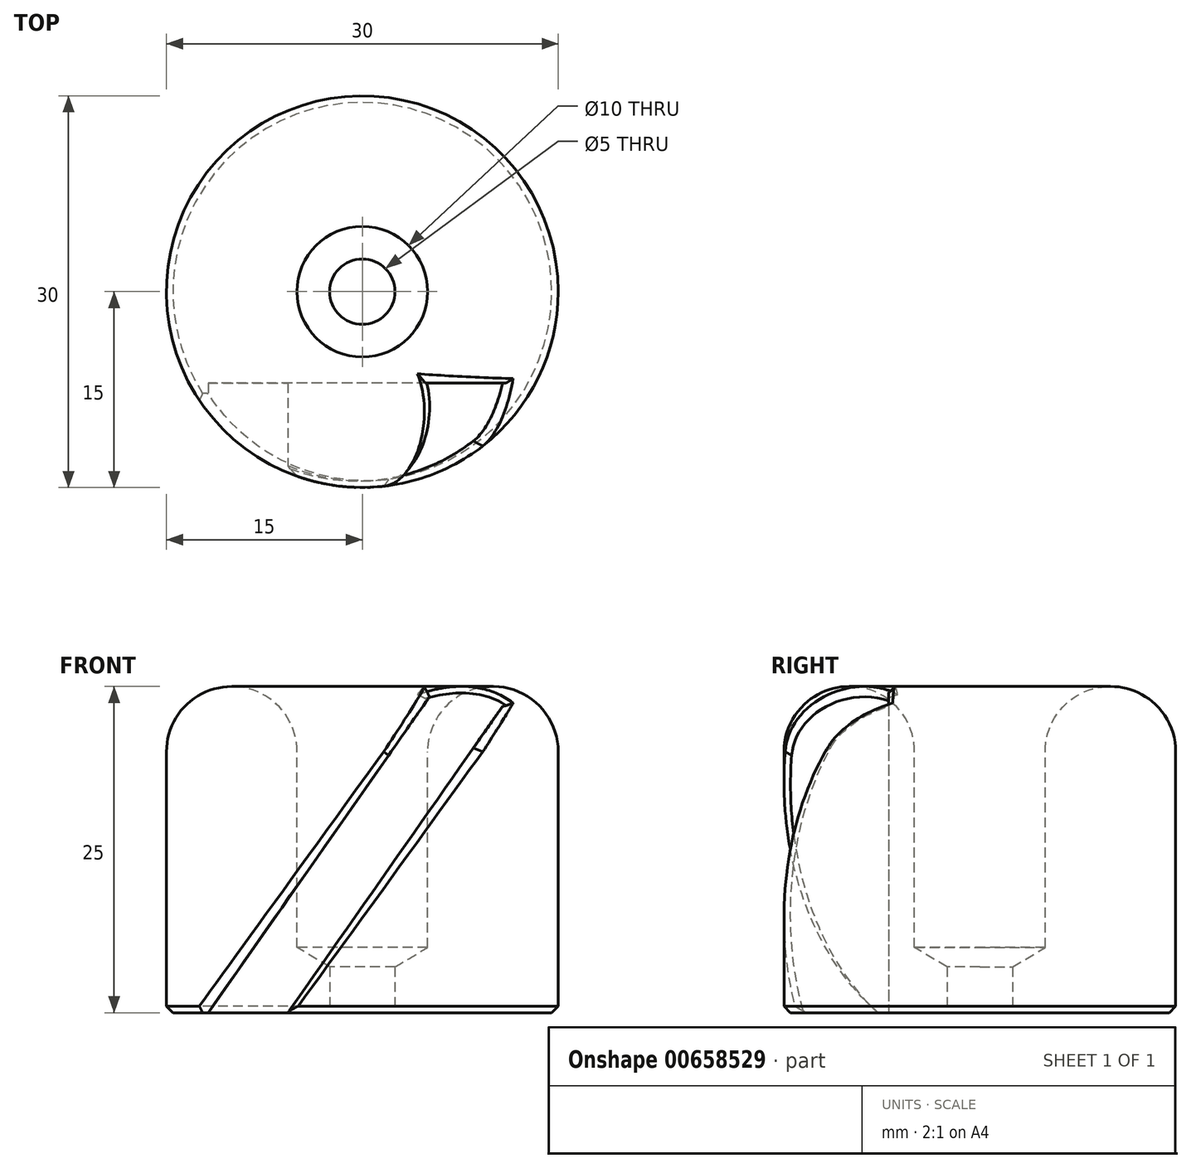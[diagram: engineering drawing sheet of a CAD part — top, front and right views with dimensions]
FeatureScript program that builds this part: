
annotation { "Feature Type Name" : "Feature", "Feature Type Description" : "" }
export const myFeature = defineFeature(function(context is Context, id is Id, definition is map)
    precondition{}
    {
        {
            var Q0;
            Q0=qCreatedBy(makeId("Top.planeOp"),FACE);
            var sketch = newSketch(context, id + "F0", { "sketchPlane" : qUnion([Q0])});
            skCircle(sketch, "E0", {"center": v(0, 0) * mm, "radius": 15 * mm});
            skLineSegment(sketch, "E1", {"start": v(-6.78, 7.35) * mm, "end": v(-2.97, -9.55) * mm, "construction": true});
            skLineSegment(sketch, "E2", {"start": v(-2.97, -9.55) * mm, "end": v(9.76, 2.2) * mm, "construction": true});
            skLineSegment(sketch, "E3", {"start": v(9.76, 2.2) * mm, "end": v(-6.78, 7.35) * mm, "construction": true});
            skCircle(sketch, "E4", {"center": v(0, 0) * mm, "radius": 10 * mm, "construction": true});
            skSolve(sketch);
        }
        {
            var Q0;
            Q0=qCreatedBy(makeId("Front.planeOp"),FACE);
            var sketch = newSketch(context, id + "F1", { "sketchPlane" : qUnion([Q0])});
            skLineSegment(sketch, "E5", {"start": v(0, 61.56) * mm, "end": v(0, 0) * mm});
            skSolve(sketch);
        }
        {
            var Q0;
            Q0=makeQuery(id+"F0.imprint","IMPRINT",FACE,{"disambiguationData":[TD([[makeQuery(id+"F0.imprint","IMPRINT",EDGE,{"derivedFrom":sQuery(id+"F0.wireOp",EDGE,"E0")}),1.0]])]});
            extrude(context, id + "F2", {"entities" : qUnion([Q0]), "depth" : 25 * mm, "offsetDistance" : 25 * mm});
        }
        {
            var Q0;
            Q0=qCreatedBy(makeId("Front.planeOp"),FACE);
            cPlane(context, id + "F3", {"entities" : qUnion([Q0]), "cplaneType" : CPlaneType.OFFSET, "offset" : 15 * mm, "width" : 150 * mm, "height" : 150 * mm});
        }
        {
            var Q0;
            Q0=qCreatedBy(id+"F3.planeOp",FACE);
            var sketch = newSketch(context, id + "F4", { "sketchPlane" : qUnion([Q0])});
            skPoint(sketch, "E6", {"position": v(0, 12.5) * mm});
            skLineSegment(sketch, "E7.bottom", {"start": v(7.7, 27.87) * mm, "end": v(11.8, 25) * mm});
            skLineSegment(sketch, "E7.top", {"start": v(-11.8, 0) * mm, "end": v(-7.7, -2.87) * mm});
            skLineSegment(sketch, "E7.left", {"start": v(7.7, 27.87) * mm, "end": v(-11.8, 0) * mm});
            skLineSegment(sketch, "E7.right", {"start": v(11.8, 25) * mm, "end": v(-7.7, -2.87) * mm});
            skLineSegment(sketch, "E8", {"start": v(-15, 0) * mm, "end": v(-15, 25) * mm});
            skLineSegment(sketch, "E9", {"start": v(15, 25) * mm, "end": v(15, 0) * mm});
            skLineSegment(sketch, "E10", {"start": v(-15, 25) * mm, "end": v(15, 25) * mm, "construction": true});
            skLineSegment(sketch, "E11", {"start": v(-15, 0) * mm, "end": v(15, 0) * mm, "construction": true});
            skPoint(sketch, "E12", {"position": v(5.7, 25) * mm});
            skPoint(sketch, "E13", {"position": v(-5.7, 0) * mm});
            skLineSegment(sketch, "E14", {"start": v(5.7, 25) * mm, "end": v(9.8, 22.13) * mm, "construction": true});
            skLineSegment(sketch, "E15", {"start": v(9.8, 22.13) * mm, "end": v(-5.7, 0) * mm});
            skSolve(sketch);
        }
        {
            var Q0;
            Q0=makeQuery(id+"F2.opExtrude","CAP_FACE",FACE,{"disambiguationData":[OSD([sQuery(id+"F0.wireOp",EDGE,"E0")])],"isStart":false});
            var sketch = newSketch(context, id + "F5", { "sketchPlane" : qUnion([Q0])});
            skPoint(sketch, "E16", {"position": v(0, 0) * mm});
            skSolve(sketch);
        }
        {
            var Q0;
            Q0=sQuery(id+"F5.wireOp",VERTEX,"E16");
            var Q1;
            Q1=makeQuery(id+"F2.opExtrude","SWEPT_BODY",BODY,{"disambiguationData":[OSD([sQuery(id+"F0.wireOp",EDGE,"E0")])]});
            hole(context, id + "F6", {"style" : HoleStyle.SIMPLE, "endStyle" : HoleEndStyle.BLIND, "holeDiameter" : 10 * mm, "majorDiameter" : 5 * mm, "holeDepth" : 20 * mm, "isTappedThrough" : true, "tappedDepth" : 12 * mm, "tapClearance" : 3, "locations" : qUnion([Q0]), "scope" : qUnion([Q1])});
        }
        {
            var Q0;
            Q0=makeQuery(id+"F2.opExtrude","CAP_FACE",FACE,{"disambiguationData":[OSD([sQuery(id+"F0.wireOp",EDGE,"E0")])],"isStart":false});
            fillet(context, id + "F7", {"entities" : qUnion([Q0]), "radius" : 5 * mm, "tangentPropagation" : true, "allowEdgeOverflow" : false});
        }
        {
            var Q0;
            Q0=makeQuery(id+"F4.imprint","IMPRINT",FACE,{"disambiguationData":[TD([[makeQuery(id+"F4.imprint","IMPRINT",EDGE,{"derivedFrom":sQuery(id+"F4.wireOp",EDGE,"E7.bottom")}),-1.0]])]});
            extrude(context, id + "F8", {"entities" : qUnion([Q0]), "operationType" : NewBodyOperationType.REMOVE, "oppositeDirection" : true, "depth" : 8 * mm, "offsetDistance" : 25 * mm});
        }
        {
            var Q0;
            Q0=sQuery(id+"F0.wireOp",VERTEX,"E0.center");
            var Q1;
            Q1=makeQuery(id+"F2.opExtrude","SWEPT_BODY",BODY,{"disambiguationData":[OSD([sQuery(id+"F0.wireOp",EDGE,"E0")])]});
            hole(context, id + "F9", {"style" : HoleStyle.SIMPLE, "endStyle" : HoleEndStyle.BLIND, "oppositeDirection" : true, "holeDiameter" : 5 * mm, "majorDiameter" : 5 * mm, "holeDepth" : 5 * mm, "isTappedThrough" : true, "tappedDepth" : 12 * mm, "tapClearance" : 3, "locations" : qUnion([Q0]), "scope" : qUnion([Q1])});
        }
        {
            var Q0;
            {var subQ0=sQuery(id+"F0.wireOp",EDGE,"E0");var subQ3=makeQuery(id+"F8.boolean.opBoolean","COPY",FACE,{"derivedFrom":makeQuery(id+"F8.opExtrude","SWEPT_FACE",FACE,{"disambiguationData":[OSD([sQuery(id+"F4.wireOp",EDGE,"E7.right")])]})});Q0=makeQuery(id+"Flb02njD701gwQ3_1.2.F8.boolean.opBoolean","SPLIT",FACE,{"disambiguationData":[TD([subQ3])],"derivedFrom":makeQuery(id+"Flb02njD701gwQ3_1.1.F8.boolean.opBoolean","SPLIT",FACE,{"disambiguationData":[TD([subQ3])],"derivedFrom":makeQuery(id+"F2.opExtrude","SWEPT_FACE",FACE,{"disambiguationData":[OSD([subQ0])]})})});}
            var Q1;
            {var subQ0=sQuery(id+"F0.wireOp",EDGE,"E0");var subQ3=makeQuery(id+"Flb02njD701gwQ3_1.1.F8.opExtrude","SWEPT_FACE",FACE,{"disambiguationData":[OSD([sQuery(id+"F4.wireOp",EDGE,"E7.left")])]});var subQ4=sQuery(id+"F4.wireOp",EDGE,"E7.right");Q1=makeQuery(id+"Flb02njD701gwQ3_1.2.F8.boolean.opBoolean","SPLIT",FACE,{"disambiguationData":[TD([makeQuery(id+"Flb02njD701gwQ3_1.1.F8.boolean.opBoolean","COPY",FACE,{"derivedFrom":subQ3})])],"derivedFrom":makeQuery(id+"Flb02njD701gwQ3_1.1.F8.boolean.opBoolean","SPLIT",FACE,{"disambiguationData":[TD([makeQuery(id+"F8.boolean.opBoolean","COPY",FACE,{"derivedFrom":makeQuery(id+"F8.opExtrude","SWEPT_FACE",FACE,{"disambiguationData":[OSD([subQ4])]})})])],"derivedFrom":makeQuery(id+"F2.opExtrude","SWEPT_FACE",FACE,{"disambiguationData":[OSD([subQ0])]})})});}
            var Q2;
            {var subQ0=sQuery(id+"F0.wireOp",EDGE,"E0");Q2=makeQuery(id+"Flb02njD701gwQ3_1.1.F8.boolean.opBoolean","SPLIT",FACE,{"disambiguationData":[TD([makeQuery(id+"F8.boolean.opBoolean","COPY",FACE,{"derivedFrom":makeQuery(id+"F8.opExtrude","SWEPT_FACE",FACE,{"disambiguationData":[OSD([sQuery(id+"F4.wireOp",EDGE,"E7.left")])]})})])],"derivedFrom":makeQuery(id+"F2.opExtrude","SWEPT_FACE",FACE,{"disambiguationData":[OSD([subQ0])]})});}
            var Q3;
            Q3=makeQuery(id+"F9.hole-0.boolean.opBoolean","COPY",EDGE,{"derivedFrom":makeQuery(id+"F9.hole-0.opRevolve","SWEPT_EDGE",EDGE,{"disambiguationData":[OSD([sQuery(id+"F9.hole-0.sketch.wireOp",EDGE,"core_line_2"),sQuery(id+"F9.hole-0.sketch.wireOp",EDGE,"core_line_3")])]})});
            var Q4;
            Q4=makeQuery(id+"Flb02njD701gwQ3_1.2.F8.boolean.opBoolean","INTERSECT",EDGE,{"derivedFrom":[makeQuery(id+"F7.opFillet","BLEND_FACE",FACE,{"disambiguationData":[OSD([sQuery(id+"F0.wireOp",EDGE,"E0")])]}),makeQuery(id+"Flb02njD701gwQ3_1.2.F8.opExtrude","CAP_FACE",FACE,{"disambiguationData":[OSD([sQuery(id+"F4.wireOp",EDGE,"E7.bottom"),sQuery(id+"F4.wireOp",EDGE,"E7.top"),sQuery(id+"F4.wireOp",EDGE,"E7.left"),sQuery(id+"F4.wireOp",EDGE,"E7.right"),sQuery(id+"F4.wireOp",EDGE,"E15")])],"isStart":false})]});
            var Q5;
            Q5=makeQuery(id+"F8.boolean.opBoolean","INTERSECT",EDGE,{"derivedFrom":[makeQuery(id+"F7.opFillet","BLEND_FACE",FACE,{"disambiguationData":[OSD([sQuery(id+"F0.wireOp",EDGE,"E0")])]}),makeQuery(id+"F8.opExtrude","CAP_FACE",FACE,{"disambiguationData":[OSD([sQuery(id+"F4.wireOp",EDGE,"E7.bottom"),sQuery(id+"F4.wireOp",EDGE,"E7.top"),sQuery(id+"F4.wireOp",EDGE,"E7.left"),sQuery(id+"F4.wireOp",EDGE,"E7.right"),sQuery(id+"F4.wireOp",EDGE,"E15")])],"isStart":false})]});
            var Q6;
            Q6=makeQuery(id+"Flb02njD701gwQ3_1.1.F8.boolean.opBoolean","INTERSECT",EDGE,{"derivedFrom":[makeQuery(id+"F7.opFillet","BLEND_FACE",FACE,{"disambiguationData":[OSD([sQuery(id+"F0.wireOp",EDGE,"E0")])]}),makeQuery(id+"Flb02njD701gwQ3_1.1.F8.opExtrude","CAP_FACE",FACE,{"disambiguationData":[OSD([sQuery(id+"F4.wireOp",EDGE,"E7.bottom"),sQuery(id+"F4.wireOp",EDGE,"E7.top"),sQuery(id+"F4.wireOp",EDGE,"E7.left"),sQuery(id+"F4.wireOp",EDGE,"E7.right"),sQuery(id+"F4.wireOp",EDGE,"E15")])],"isStart":false})]});
            chamfer(context, id + "F10", {"entities" : qUnion([Q0, Q1, Q2, Q3, Q4, Q5, Q6]), "width" : 0.5 * mm, "tangentPropagation" : true});
        }
    });
